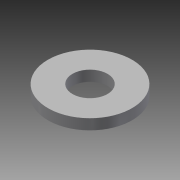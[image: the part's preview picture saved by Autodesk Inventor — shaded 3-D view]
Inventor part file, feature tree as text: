
AUTODESK INVENTOR PART (.ipt)
format: ipt  version: 2014 SP1 (Build 180222100, 222)  size: 75,776 bytes
history: native  units: in
note: dims shown in document units (in); Inventor stores cm internally (conversion verified against a paired STEP export)
features: extrude x1, sketch x1
ambient origin geometry x8: Origin, YZ Plane, XZ Plane, XY Plane, X Axis, Y Axis, Z Axis, Center Point
bodies: Solid1 (feature_tree)
feature tree (2):
  extrude  "Extrusion1"  Depth=0.0469in
  sketch  "Sketch1"  dims[d0=0.1562in d1=0.375in d2=0.0469in d3=0.0in]
